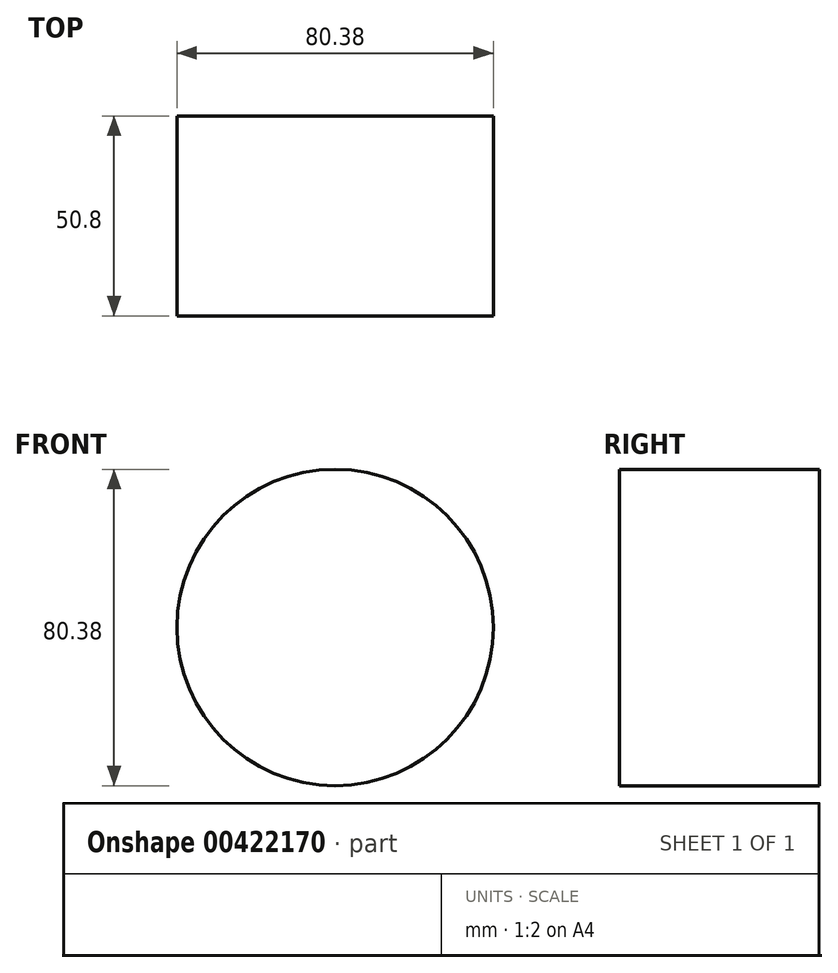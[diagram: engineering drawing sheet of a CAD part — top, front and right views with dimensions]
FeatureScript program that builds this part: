
annotation { "Feature Type Name" : "Feature", "Feature Type Description" : "" }
export const myFeature = defineFeature(function(context is Context, id is Id, definition is map)
    precondition{}
    {
        {
            var Q0;
            Q0=qCreatedBy(makeId("Front.planeOp"),FACE);
            var sketch = newSketch(context, id + "F0", { "sketchPlane" : qUnion([Q0])});
            skCircle(sketch, "E0", {"center": v(0, 0) * mm, "radius": 40.2 * mm});
            skSolve(sketch);
        }
        {
            var Q0;
            Q0=makeQuery(id+"F0.imprint","IMPRINT",FACE,{"disambiguationData":[TD([[makeQuery(id+"F0.imprint","IMPRINT",EDGE,{"derivedFrom":sQuery(id+"F0.wireOp",EDGE,"E0")}),1.0]])]});
            extrude(context, id + "F1", {"entities" : qUnion([Q0]), "depth" : 25.4 * mm});
        }
        {
            var Q0;
            Q0=makeQuery(id+"F1.opExtrude","CAP_FACE",FACE,{"disambiguationData":[OSD([sQuery(id+"F0.wireOp",EDGE,"E0")])],"isStart":false});
            var Q1;
            Q1=makeQuery(id+"F1.opExtrude","CAP_FACE",FACE,{"disambiguationData":[OSD([sQuery(id+"F0.wireOp",EDGE,"E0")])],"isStart":true});
            extrude(context, id + "F2", {"entities" : qUnion([Q0, Q1]), "operationType" : NewBodyOperationType.ADD, "depth" : 25.4 * mm});
        }
    });
